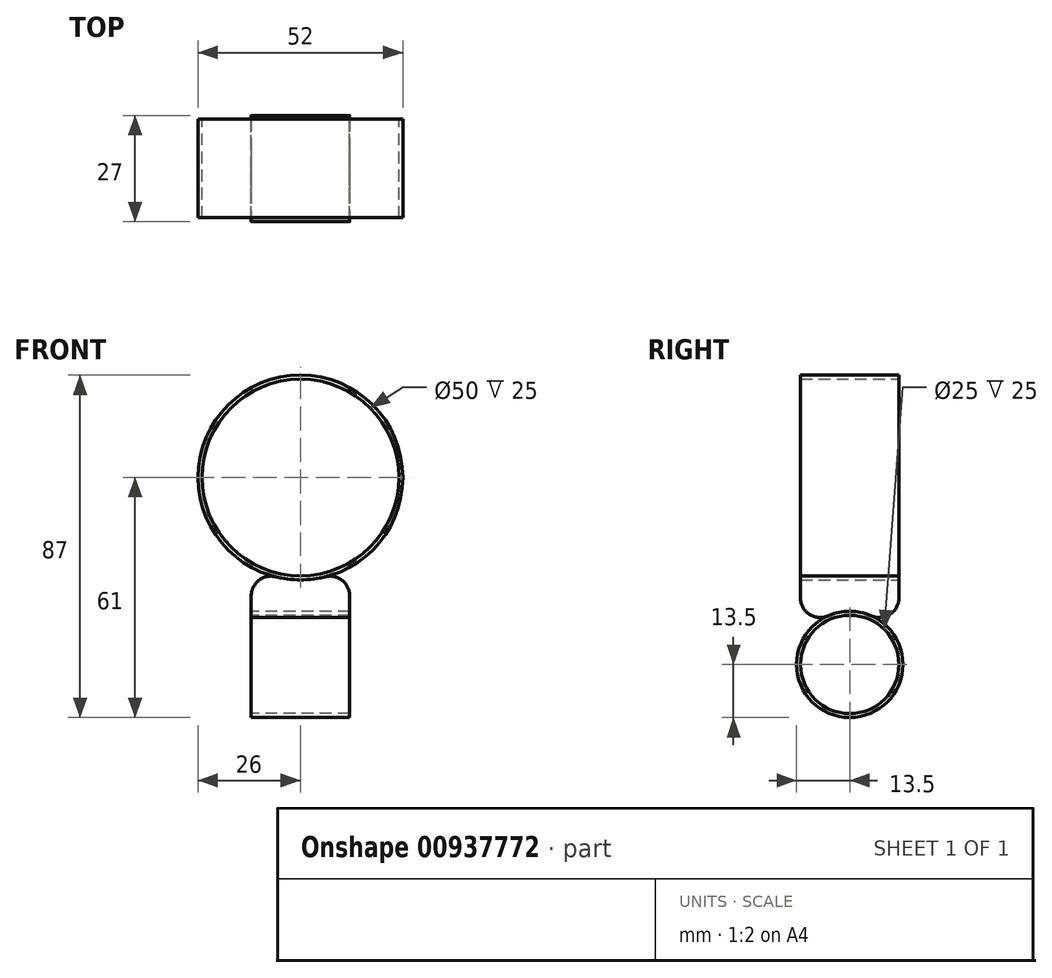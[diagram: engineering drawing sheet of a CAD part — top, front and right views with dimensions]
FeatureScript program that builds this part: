
annotation { "Feature Type Name" : "Feature", "Feature Type Description" : "" }
export const myFeature = defineFeature(function(context is Context, id is Id, definition is map)
    precondition{}
    {
        {
            var Q0;
            Q0=qCreatedBy(makeId("Front.planeOp"),FACE);
            var sketch = newSketch(context, id + "F0", { "sketchPlane" : qUnion([Q0])});
            skArc(sketch, "E0", {"start": v(0, 50) * mm, "mid": v(-25, 25) * mm, "end": v(0, 0) * mm});
            skArc(sketch, "E1.MirrorCS", {"start": v(0, 50) * mm, "mid": v(25, 25) * mm, "end": v(0, 0) * mm});
            skCircle(sketch, "E2", {"center": v(0, 25) * mm, "radius": 26 * mm});
            skSolve(sketch);
        }
        {
            var Q0;
            Q0=qCreatedBy(makeId("Right.planeOp"),FACE);
            var sketch = newSketch(context, id + "F1", { "sketchPlane" : qUnion([Q0])});
            skPoint(sketch, "E3", {"position": v(0, -10) * mm});
            skArc(sketch, "E4", {"start": v(0, -10) * mm, "mid": v(-12.5, -22.5) * mm, "end": v(0, -35) * mm});
            skArc(sketch, "E5.MirrorCS", {"start": v(0, -10) * mm, "mid": v(12.5, -22.5) * mm, "end": v(0, -35) * mm});
            skCircle(sketch, "E6", {"center": v(0, -22.5) * mm, "radius": 13.5 * mm});
            skSolve(sketch);
        }
        {
            var Q0;
            Q0=makeQuery(id+"F0.imprint","IMPRINT",FACE,{"disambiguationData":[TD([[makeQuery(id+"F0.imprint","IMPRINT",EDGE,{"derivedFrom":sQuery(id+"F0.wireOp",EDGE,"E0")}),-1.0]])]});
            extrude(context, id + "F2", {"entities" : qUnion([Q0]), "depth" : 25 * mm, "offsetDistance" : 25 * mm, "symmetric" : true});
        }
        {
            var Q0;
            Q0=makeQuery(id+"F1.imprint","IMPRINT",FACE,{"disambiguationData":[TD([[makeQuery(id+"F1.imprint","IMPRINT",EDGE,{"derivedFrom":sQuery(id+"F1.wireOp",EDGE,"E4")}),-1.0]])]});
            extrude(context, id + "F3", {"entities" : qUnion([Q0]), "depth" : 25 * mm, "offsetDistance" : 25 * mm, "symmetric" : true});
        }
        {
            var Q0;
            Q0=qCreatedBy(makeId("Top.planeOp"),FACE);
            cPlane(context, id + "F4", {"entities" : qUnion([Q0]), "cplaneType" : CPlaneType.OFFSET, "offset" : 2 * mm, "oppositeDirection" : true, "width" : 150 * mm, "height" : 150 * mm});
        }
        {
            var Q0;
            Q0=qCreatedBy(id+"F4.planeOp",FACE);
            var sketch = newSketch(context, id + "F5", { "sketchPlane" : qUnion([Q0])});
            skLineSegment(sketch, "E7.bottom", {"start": v(-12.5, -12.5) * mm, "end": v(12.5, -12.5) * mm});
            skLineSegment(sketch, "E7.top", {"start": v(-12.5, 12.5) * mm, "end": v(12.5, 12.5) * mm});
            skLineSegment(sketch, "E7.left", {"start": v(-12.5, -12.5) * mm, "end": v(-12.5, 12.5) * mm});
            skLineSegment(sketch, "E7.right", {"start": v(12.5, -12.5) * mm, "end": v(12.5, 12.5) * mm});
            skPoint(sketch, "E7.middle", {"position": v(0, 0) * mm});
            skSolve(sketch);
        }
        {
            var Q0;
            Q0=makeQuery(id+"F5.imprint","IMPRINT",FACE,{"disambiguationData":[TD([[makeQuery(id+"F5.imprint","IMPRINT",EDGE,{"derivedFrom":sQuery(id+"F5.wireOp",EDGE,"E7.bottom")}),1.0]])]});
            extrude(context, id + "F6", {"entities" : qUnion([Q0]), "endBound" : BoundingType.UP_TO_NEXT, "oppositeDirection" : true, "depth" : 25 * mm, "offsetDistance" : 25 * mm, "hasSecondDirection" : true, "secondDirectionBound" : BoundingType.UP_TO_NEXT, "secondDirectionOppositeDirection" : false, "secondDirectionDepth" : 25 * mm});
        }
        {
            var Q0;
            Q0=makeQuery(id+"F6.opExtrude","CAP_EDGE",EDGE,{"disambiguationData":[OSD([sQuery(id+"F5.wireOp",EDGE,"E7.left")])],"isStart":false});
            var Q1;
            Q1=makeQuery(id+"F6.opExtrude","CAP_EDGE",EDGE,{"disambiguationData":[OSD([sQuery(id+"F5.wireOp",EDGE,"E7.right")]),topologyDisambiguationEdgeConnected([makeQuery(id+"F2.opExtrude","SWEPT_FACE",FACE,{"disambiguationData":[OSD([sQuery(id+"F0.wireOp",EDGE,"E2")])]})])],"isStart":false});
            var Q2;
            Q2=makeQuery(id+"F6.opExtrude","CAP_EDGE",EDGE,{"disambiguationData":[OSD([sQuery(id+"F5.wireOp",EDGE,"E7.bottom")]),topologyDisambiguationEdgeConnected([makeQuery(id+"F3.opExtrude","SWEPT_FACE",FACE,{"disambiguationData":[OSD([sQuery(id+"F1.wireOp",EDGE,"E6")])]})])],"isStart":false});
            var Q3;
            Q3=makeQuery(id+"F6.opExtrude","CAP_EDGE",EDGE,{"disambiguationData":[OSD([sQuery(id+"F5.wireOp",EDGE,"E7.top")])],"isStart":false});
            fillet(context, id + "F7", {"entities" : qUnion([Q0, Q1, Q2, Q3]), "radius" : 5 * mm, "tangentPropagation" : true, "allowEdgeOverflow" : false});
        }
    });
